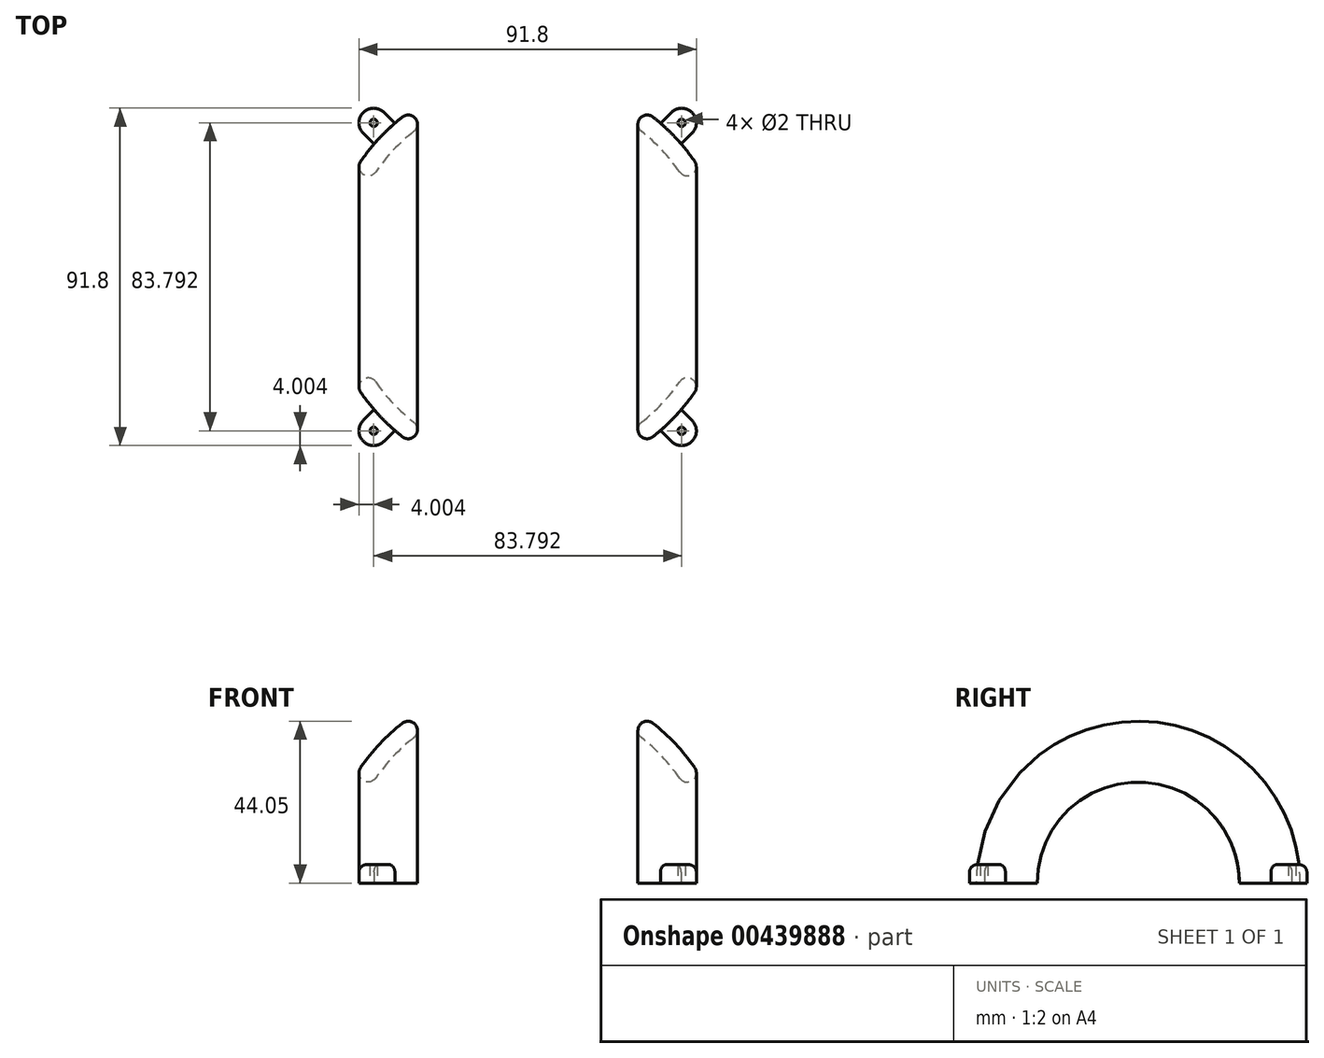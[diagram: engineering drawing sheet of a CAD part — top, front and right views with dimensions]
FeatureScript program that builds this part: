
annotation { "Feature Type Name" : "Feature", "Feature Type Description" : "" }
export const myFeature = defineFeature(function(context is Context, id is Id, definition is map)
    precondition{}
    {
        {
            var Q0;
            Q0=qCreatedBy(makeId("Top.planeOp"),FACE);
            var sketch = newSketch(context, id + "F0", { "sketchPlane" : qUnion([Q0])});
            skArc(sketch, "E0", {"start": v(55.25, 0) * mm, "mid": v(0, 55.25) * mm, "end": v(-55.25, 0) * mm});
            skLineSegment(sketch, "E1", {"start": v(-55.25, 0) * mm, "end": v(55.25, 0) * mm});
            skSolve(sketch);
        }
        {
            var Q0;
            Q0=makeQuery(id+"F0.imprint","IMPRINT",FACE,{"disambiguationData":[TD([[makeQuery(id+"F0.imprint","IMPRINT",EDGE,{"derivedFrom":sQuery(id+"F0.wireOp",EDGE,"E0")}),1.0]])]});
            var Q1;
            Q1=sQuery(id+"F0.wireOp",EDGE,"E1");
            revolve(context, id + "F1", {"entities" : qUnion([Q0]), "axis" : qUnion([Q1]), "revolveType" : RevolveType.ONE_DIRECTION, "angle" : 180 * degree});
        }
        {
            var Q0;
            Q0=makeQuery(id+"F1.opRevolve","CAP_FACE",FACE,{"disambiguationData":[OSD([sQuery(id+"F0.wireOp",EDGE,"E0"),sQuery(id+"F0.wireOp",EDGE,"E1")])],"isStart":true});
            shell(context, id + "F2", {"entities" : qUnion([Q0]), "thickness" : 5 * mm});
        }
        {
            var Q0;
            Q0=qCreatedBy(makeId("Right.planeOp"),FACE);
            var sketch = newSketch(context, id + "F3", { "sketchPlane" : qUnion([Q0])});
            skCircle(sketch, "E2", {"center": v(0, 0) * mm, "radius": 27.5 * mm});
            skSolve(sketch);
        }
        {
            var Q0;
            Q0 = qSketchRegion(id + "F3", true);
            extrude(context, id + "F4", {"entities" : qUnion([Q0]), "operationType" : NewBodyOperationType.REMOVE, "endBound" : BoundingType.SYMMETRIC, "depth" : 188 * mm});
        }
        {
            var Q0;
            Q0=makeQuery(id+"F4.boolean.opBoolean","INTERSECT",EDGE,{"disambiguationData":[OD(1.0)],"derivedFrom":[makeQuery(id+"F1.opRevolve","SWEPT_FACE",FACE,{"disambiguationData":[OSD([sQuery(id+"F0.wireOp",EDGE,"E0")])]}),makeQuery(id+"F4.opExtrude","SWEPT_FACE",FACE,{"disambiguationData":[OSD([sQuery(id+"F3.wireOp",EDGE,"E2")])]})]});
            var Q1;
            Q1=makeQuery(id+"F4.boolean.opBoolean","INTERSECT",EDGE,{"disambiguationData":[OD(0.0)],"derivedFrom":[makeQuery(id+"F2.opShell","OFFSET_FACE",FACE,{"disambiguationData":[OSD([sQuery(id+"F0.wireOp",EDGE,"E0")])]}),makeQuery(id+"F4.opExtrude","SWEPT_FACE",FACE,{"disambiguationData":[OSD([sQuery(id+"F3.wireOp",EDGE,"E2")])]})]});
            var Q2;
            Q2=makeQuery(id+"F4.boolean.opBoolean","INTERSECT",EDGE,{"disambiguationData":[OD(0.0)],"derivedFrom":[makeQuery(id+"F1.opRevolve","SWEPT_FACE",FACE,{"disambiguationData":[OSD([sQuery(id+"F0.wireOp",EDGE,"E0")])]}),makeQuery(id+"F4.opExtrude","SWEPT_FACE",FACE,{"disambiguationData":[OSD([sQuery(id+"F3.wireOp",EDGE,"E2")])]})]});
            var Q3;
            Q3=makeQuery(id+"F4.boolean.opBoolean","INTERSECT",EDGE,{"disambiguationData":[OD(1.0)],"derivedFrom":[makeQuery(id+"F2.opShell","OFFSET_FACE",FACE,{"disambiguationData":[OSD([sQuery(id+"F0.wireOp",EDGE,"E0")])]}),makeQuery(id+"F4.opExtrude","SWEPT_FACE",FACE,{"disambiguationData":[OSD([sQuery(id+"F3.wireOp",EDGE,"E2")])]})]});
            fillet(context, id + "F5", {"entities" : qUnion([Q0, Q1, Q2, Q3]), "radius" : 2.5 * mm, "tangentPropagation" : true, "allowEdgeOverflow" : false});
        }
        {
            var Q0;
            Q0=qCreatedBy(makeId("Front.planeOp"),FACE);
            var sketch = newSketch(context, id + "F6", { "sketchPlane" : qUnion([Q0])});
            skLineSegment(sketch, "E3.bottom", {"start": v(30, -1.6) * mm, "end": v(-30, -1.6) * mm});
            skLineSegment(sketch, "E3.top", {"start": v(30, 94.44) * mm, "end": v(-30, 94.44) * mm});
            skLineSegment(sketch, "E3.left", {"start": v(30, -1.6) * mm, "end": v(30, 94.44) * mm});
            skLineSegment(sketch, "E3.right", {"start": v(-30, -1.6) * mm, "end": v(-30, 94.44) * mm});
            skSolve(sketch);
        }
        {
            var Q0;
            Q0 = qSketchRegion(id + "F6", true);
            extrude(context, id + "F7", {"entities" : qUnion([Q0]), "operationType" : NewBodyOperationType.REMOVE, "endBound" : BoundingType.SYMMETRIC, "oppositeDirection" : true, "depth" : 129.4 * mm});
        }
        {
            var Q0;
            Q0=makeQuery(id+"F7.boolean.opBoolean","INTERSECT",EDGE,{"derivedFrom":[makeQuery(id+"F1.opRevolve","SWEPT_FACE",FACE,{"disambiguationData":[OSD([sQuery(id+"F0.wireOp",EDGE,"E0")])]}),makeQuery(id+"F7.opExtrude","SWEPT_FACE",FACE,{"disambiguationData":[OSD([sQuery(id+"F6.wireOp",EDGE,"E3.left")])]})]});
            var Q1;
            Q1=makeQuery(id+"F7.boolean.opBoolean","INTERSECT",EDGE,{"derivedFrom":[makeQuery(id+"F2.opShell","OFFSET_FACE",FACE,{"disambiguationData":[OSD([sQuery(id+"F0.wireOp",EDGE,"E0")])]}),makeQuery(id+"F7.opExtrude","SWEPT_FACE",FACE,{"disambiguationData":[OSD([sQuery(id+"F6.wireOp",EDGE,"E3.left")])]})]});
            var Q2;
            Q2=makeQuery(id+"F7.boolean.opBoolean","INTERSECT",EDGE,{"derivedFrom":[makeQuery(id+"F2.opShell","OFFSET_FACE",FACE,{"disambiguationData":[OSD([sQuery(id+"F0.wireOp",EDGE,"E0")])]}),makeQuery(id+"F7.opExtrude","SWEPT_FACE",FACE,{"disambiguationData":[OSD([sQuery(id+"F6.wireOp",EDGE,"E3.right")])]})]});
            var Q3;
            Q3=makeQuery(id+"F7.boolean.opBoolean","INTERSECT",EDGE,{"derivedFrom":[makeQuery(id+"F1.opRevolve","SWEPT_FACE",FACE,{"disambiguationData":[OSD([sQuery(id+"F0.wireOp",EDGE,"E0")])]}),makeQuery(id+"F7.opExtrude","SWEPT_FACE",FACE,{"disambiguationData":[OSD([sQuery(id+"F6.wireOp",EDGE,"E3.right")])]})]});
            fillet(context, id + "F8", {"entities" : qUnion([Q0, Q1, Q2, Q3]), "radius" : 2.5 * mm, "tangentPropagation" : true, "allowEdgeOverflow" : false});
        }
        {
            var Q0;
            Q0=qCreatedBy(makeId("Top.planeOp"),FACE);
            var sketch = newSketch(context, id + "F9", { "sketchPlane" : qUnion([Q0])});
            skCircle(sketch, "E4", {"center": v(0, 0) * mm, "radius": 55.25 * mm});
            skArc(sketch, "E5", {"start": v(-39.07, 44.72) * mm, "mid": v(-44.72, 44.72) * mm, "end": v(-44.72, 39.07) * mm});
            skArc(sketch, "E6", {"start": v(44.72, 39.07) * mm, "mid": v(44.72, 44.72) * mm, "end": v(39.07, 44.72) * mm});
            skArc(sketch, "E7", {"start": v(39.07, -44.72) * mm, "mid": v(44.72, -44.72) * mm, "end": v(44.72, -39.07) * mm});
            skArc(sketch, "E8", {"start": v(-44.72, -39.07) * mm, "mid": v(-44.72, -44.72) * mm, "end": v(-39.07, -44.72) * mm});
            skLineSegment(sketch, "E9", {"start": v(-39.07, 44.72) * mm, "end": v(-36.14, 41.8) * mm});
            skLineSegment(sketch, "E10", {"start": v(-44.72, 39.07) * mm, "end": v(-41.8, 36.14) * mm});
            skLineSegment(sketch, "E11", {"start": v(39.07, 44.72) * mm, "end": v(36.14, 41.8) * mm});
            skLineSegment(sketch, "E12", {"start": v(44.72, 39.07) * mm, "end": v(41.8, 36.14) * mm});
            skLineSegment(sketch, "E13", {"start": v(-44.72, -39.07) * mm, "end": v(-41.8, -36.14) * mm});
            skLineSegment(sketch, "E14", {"start": v(-39.07, -44.72) * mm, "end": v(-36.14, -41.8) * mm});
            skLineSegment(sketch, "E15", {"start": v(41.8, -36.14) * mm, "end": v(44.72, -39.07) * mm});
            skLineSegment(sketch, "E16", {"start": v(36.14, -41.8) * mm, "end": v(39.07, -44.72) * mm});
            skCircle(sketch, "E17", {"center": v(41.9, -41.9) * mm, "radius": 1 * mm});
            skCircle(sketch, "E18", {"center": v(-41.9, -41.9) * mm, "radius": 1 * mm});
            skCircle(sketch, "E19", {"center": v(41.9, 41.9) * mm, "radius": 1 * mm});
            skCircle(sketch, "E20", {"center": v(-41.9, 41.9) * mm, "radius": 1 * mm});
            skSolve(sketch);
        }
        {
            var Q0;
            Q0=makeQuery(id+"F9.imprint","IMPRINT",FACE,{"disambiguationData":[TD([[makeQuery(id+"F9.imprint","IMPRINT",EDGE,{"derivedFrom":sQuery(id+"F9.wireOp",EDGE,"E7")}),1.0]])]});
            var Q1;
            Q1=makeQuery(id+"F9.imprint","IMPRINT",FACE,{"disambiguationData":[TD([[makeQuery(id+"F9.imprint","IMPRINT",EDGE,{"derivedFrom":sQuery(id+"F9.wireOp",EDGE,"E6")}),1.0]])]});
            var Q2;
            Q2=makeQuery(id+"F9.imprint","IMPRINT",FACE,{"disambiguationData":[TD([[makeQuery(id+"F9.imprint","IMPRINT",EDGE,{"derivedFrom":sQuery(id+"F9.wireOp",EDGE,"E5")}),1.0]])]});
            var Q3;
            Q3=makeQuery(id+"F9.imprint","IMPRINT",FACE,{"disambiguationData":[TD([[makeQuery(id+"F9.imprint","IMPRINT",EDGE,{"derivedFrom":sQuery(id+"F9.wireOp",EDGE,"E8")}),1.0]])]});
            extrude(context, id + "F10", {"entities" : qUnion([Q0, Q1, Q2, Q3]), "operationType" : NewBodyOperationType.ADD, "depth" : 5 * mm});
        }
        {
            var Q0;
            Q0=makeQuery(id+"F10.opExtrude","CAP_EDGE",EDGE,{"disambiguationData":[OSD([sQuery(id+"F9.wireOp",EDGE,"E6")])],"isStart":false});
            var Q1;
            Q1=makeQuery(id+"F10.opExtrude","CAP_EDGE",EDGE,{"disambiguationData":[OSD([sQuery(id+"F9.wireOp",EDGE,"E5")])],"isStart":false});
            var Q2;
            Q2=makeQuery(id+"F10.opExtrude","CAP_EDGE",EDGE,{"disambiguationData":[OSD([sQuery(id+"F9.wireOp",EDGE,"E8")])],"isStart":false});
            var Q3;
            Q3=makeQuery(id+"F10.opExtrude","CAP_EDGE",EDGE,{"disambiguationData":[OSD([sQuery(id+"F9.wireOp",EDGE,"E7")])],"isStart":false});
            fillet(context, id + "F11", {"entities" : qUnion([Q0, Q1, Q2, Q3]), "radius" : 2 * mm, "tangentPropagation" : true, "allowEdgeOverflow" : false});
        }
    });
